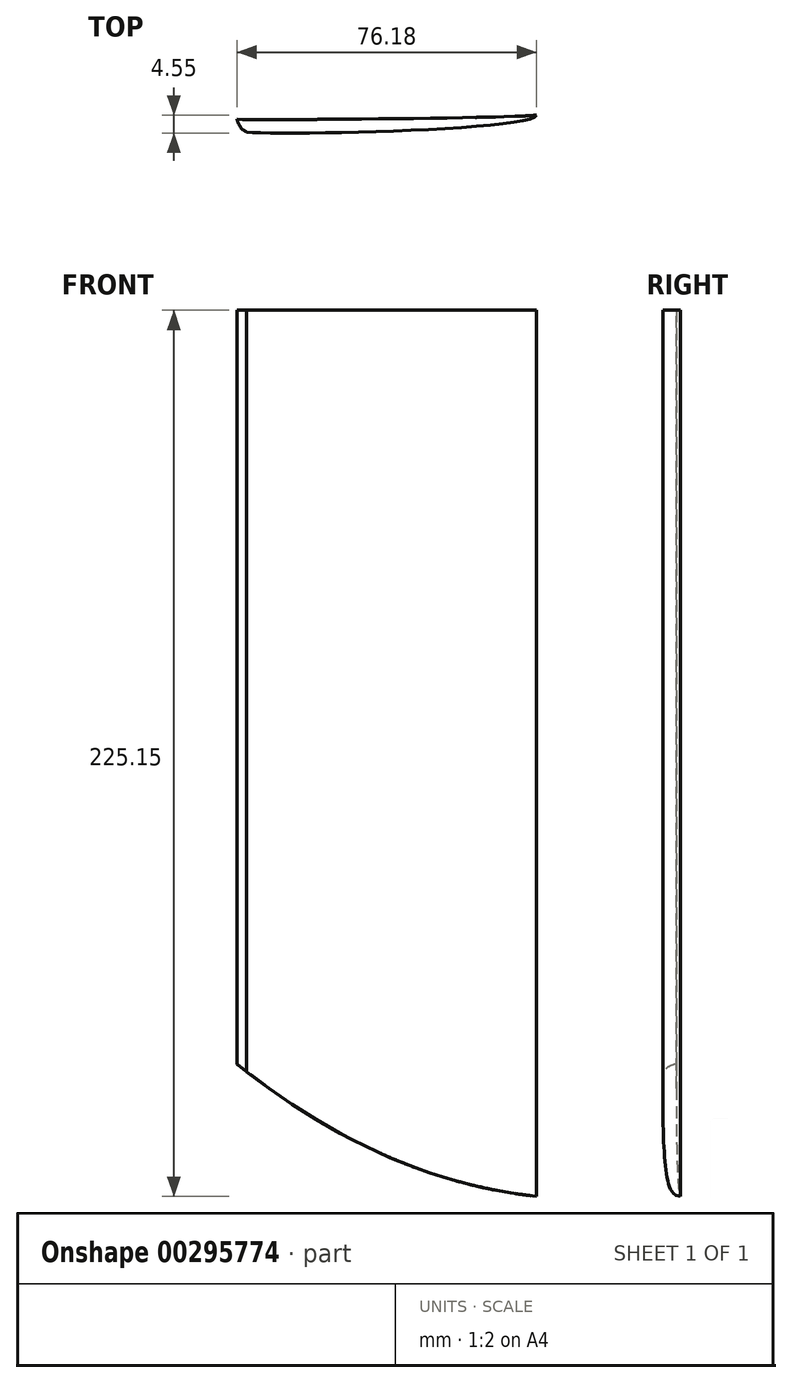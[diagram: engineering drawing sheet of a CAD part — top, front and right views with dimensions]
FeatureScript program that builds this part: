
annotation { "Feature Type Name" : "Feature", "Feature Type Description" : "" }
export const myFeature = defineFeature(function(context is Context, id is Id, definition is map)
    precondition{}
    {
        {
            var Q0;
            Q0=qCreatedBy(makeId("Top.planeOp"),FACE);
            var sketch = newSketch(context, id + "F0", { "sketchPlane" : qUnion([Q0])});
            skFitSpline(sketch, "E0", {"points": [v(-41.91, 5.74) * mm, v(34.27, 6.8) * mm], "startDerivative": vector(25.36, -0.66) * mm, "endDerivative": vector(24.25, 2.49) * mm});
            skFitSpline(sketch, "E1", {"points": [v(-41.91, 5.74) * mm, v(-39.4, 2.43) * mm], "startDerivative": vector(1.59, -4.55) * mm, "endDerivative": vector(4.95, -2.94) * mm});
            skFitSpline(sketch, "E2", {"points": [v(-39.4, 2.43) * mm, v(34.27, 6.8) * mm], "startDerivative": vector(26.96, -1.93) * mm, "endDerivative": vector(5.07, 11.98) * mm});
            skSolve(sketch);
        }
        {
            var Q0;
            Q0 = qSketchRegion(id + "F0", true);
            extrude(context, id + "F1", {"entities" : qUnion([Q0]), "depth" : 228.6 * mm});
        }
        {
            var Q0;
            Q0=qCreatedBy(makeId("Front.planeOp"),FACE);
            var sketch = newSketch(context, id + "F2", { "sketchPlane" : qUnion([Q0])});
            skFitSpline(sketch, "E3", {"points": [v(52.35, 2.79) * mm, v(-88.06, 76.05) * mm], "startDerivative": vector(-248.86, -8.37) * mm, "endDerivative": vector(-40.94, -2.15) * mm});
            skFitSpline(sketch, "E4", {"points": [v(-88.06, 76.05) * mm, v(-88.06, -22.7) * mm, v(52.35, 2.79) * mm], "startDerivative": vector(-49.9, -227.17) * mm, "endDerivative": vector(296.96, 108.44) * mm});
            skSolve(sketch);
        }
        {
            var Q0;
            Q0 = qSketchRegion(id + "F2", true);
            extrude(context, id + "F3", {"entities" : qUnion([Q0]), "operationType" : NewBodyOperationType.REMOVE, "oppositeDirection" : true, "depth" : 18.29 * mm});
        }
    });
